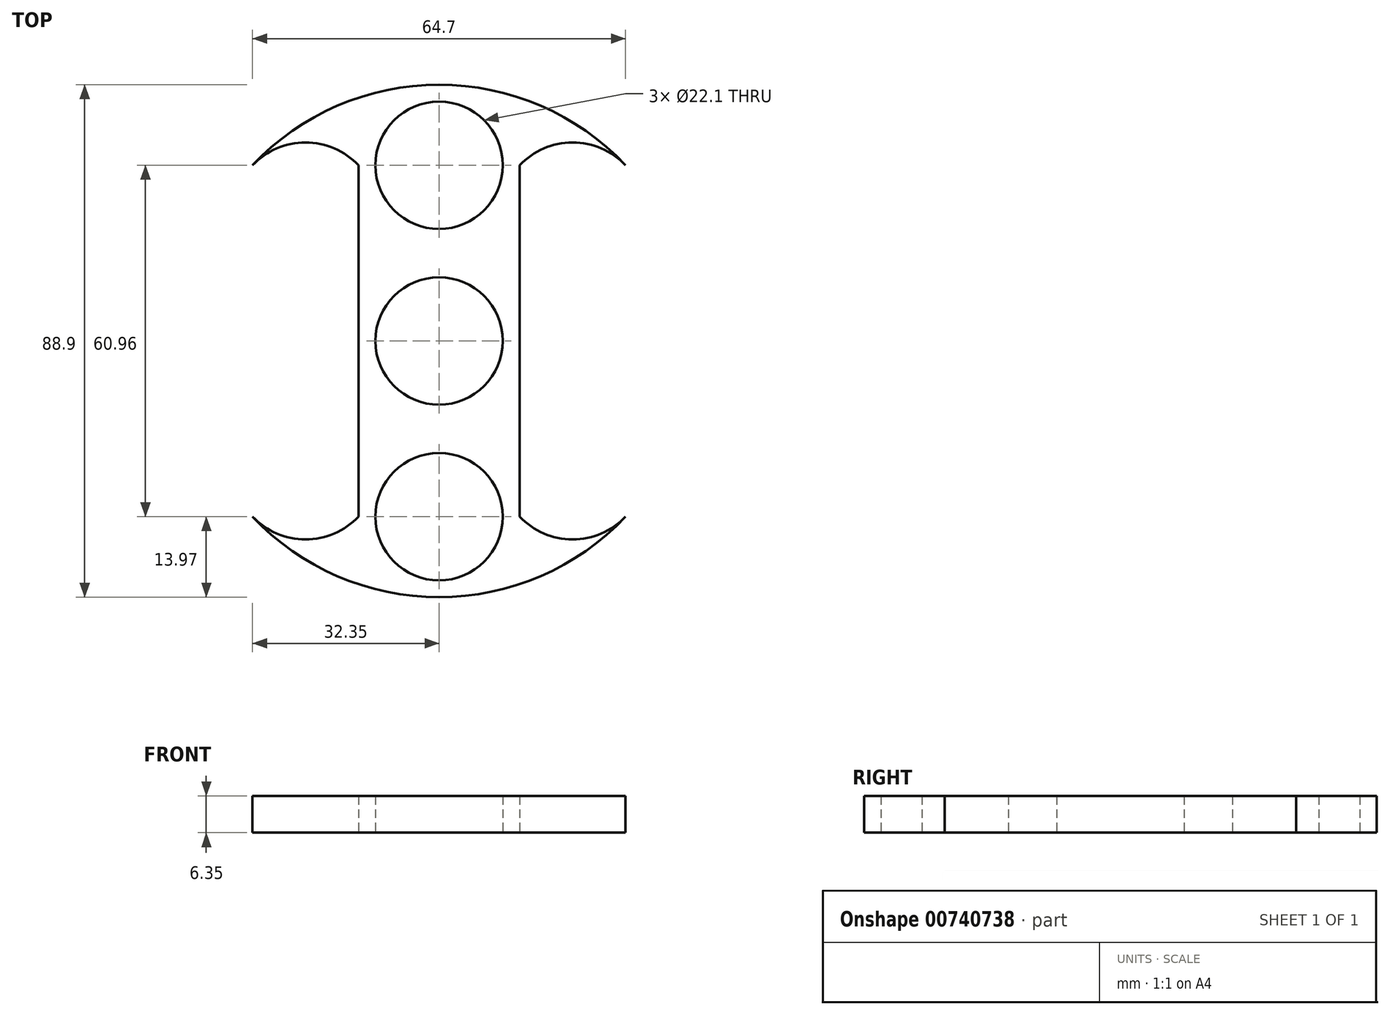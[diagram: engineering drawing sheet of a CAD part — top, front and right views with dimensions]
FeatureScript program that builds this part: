
annotation { "Feature Type Name" : "Feature", "Feature Type Description" : "" }
export const myFeature = defineFeature(function(context is Context, id is Id, definition is map)
    precondition{}
    {
        {
            var Q0;
            Q0=qCreatedBy(makeId("Top.planeOp"),FACE);
            var sketch = newSketch(context, id + "F0", { "sketchPlane" : qUnion([Q0])});
            skCircle(sketch, "E0", {"center": v(0, 0) * mm, "radius": 11.05 * mm});
            skCircle(sketch, "E1", {"center": v(0, 0) * mm, "radius": 13.97 * mm});
            skLineSegment(sketch, "E2", {"start": v(0, 0) * mm, "end": v(0, 30.48) * mm});
            skCircle(sketch, "E3", {"center": v(0, 30.48) * mm, "radius": 13.97 * mm});
            skCircle(sketch, "E4", {"center": v(0, 30.48) * mm, "radius": 11.05 * mm});
            skLineSegment(sketch, "E5", {"start": v(0, 0) * mm, "end": v(0, -30.48) * mm});
            skCircle(sketch, "E6", {"center": v(0, -30.48) * mm, "radius": 13.97 * mm});
            skCircle(sketch, "E7", {"center": v(0, -30.48) * mm, "radius": 11.05 * mm});
            skArc(sketch, "E8", {"start": v(-32.35, -30.48) * mm, "mid": v(0, -44.45) * mm, "end": v(32.35, -30.48) * mm});
            skPoint(sketch, "E9", {"position": v(-13.97, -30.48) * mm});
            skPoint(sketch, "E10", {"position": v(13.97, -30.48) * mm});
            skPoint(sketch, "E11", {"position": v(13.97, 30.48) * mm});
            skPoint(sketch, "E12", {"position": v(-13.97, 30.48) * mm});
            skArc(sketch, "E13", {"start": v(32.35, 30.48) * mm, "mid": v(23.16, 34.42) * mm, "end": v(13.97, 30.48) * mm});
            skArc(sketch, "E14", {"start": v(-13.97, 30.48) * mm, "mid": v(-23.16, 34.42) * mm, "end": v(-32.35, 30.48) * mm});
            skArc(sketch, "E15", {"start": v(13.97, -30.48) * mm, "mid": v(23.16, -34.42) * mm, "end": v(32.35, -30.48) * mm});
            skArc(sketch, "E16", {"start": v(-32.35, -30.48) * mm, "mid": v(-23.16, -34.42) * mm, "end": v(-13.97, -30.48) * mm});
            skArc(sketch, "E17.trimOffspring", {"start": v(32.35, 30.48) * mm, "mid": v(0, 44.45) * mm, "end": v(-32.35, 30.48) * mm});
            skLineSegment(sketch, "E18", {"start": v(-13.97, -30.48) * mm, "end": v(-13.97, 0) * mm});
            skLineSegment(sketch, "E19", {"start": v(-13.97, 0) * mm, "end": v(-13.97, 30.48) * mm});
            skLineSegment(sketch, "E20", {"start": v(13.97, 30.48) * mm, "end": v(13.97, 0) * mm});
            skLineSegment(sketch, "E21", {"start": v(13.97, 0) * mm, "end": v(13.97, -30.48) * mm});
            skSolve(sketch);
        }
        {
            var Q0;
            Q0 = qSketchRegion(id + "F0", true);
            extrude(context, id + "F1", {"entities" : qUnion([Q0]), "depth" : 6.35 * mm, "offsetDistance" : 25.4 * mm});
        }
    });
